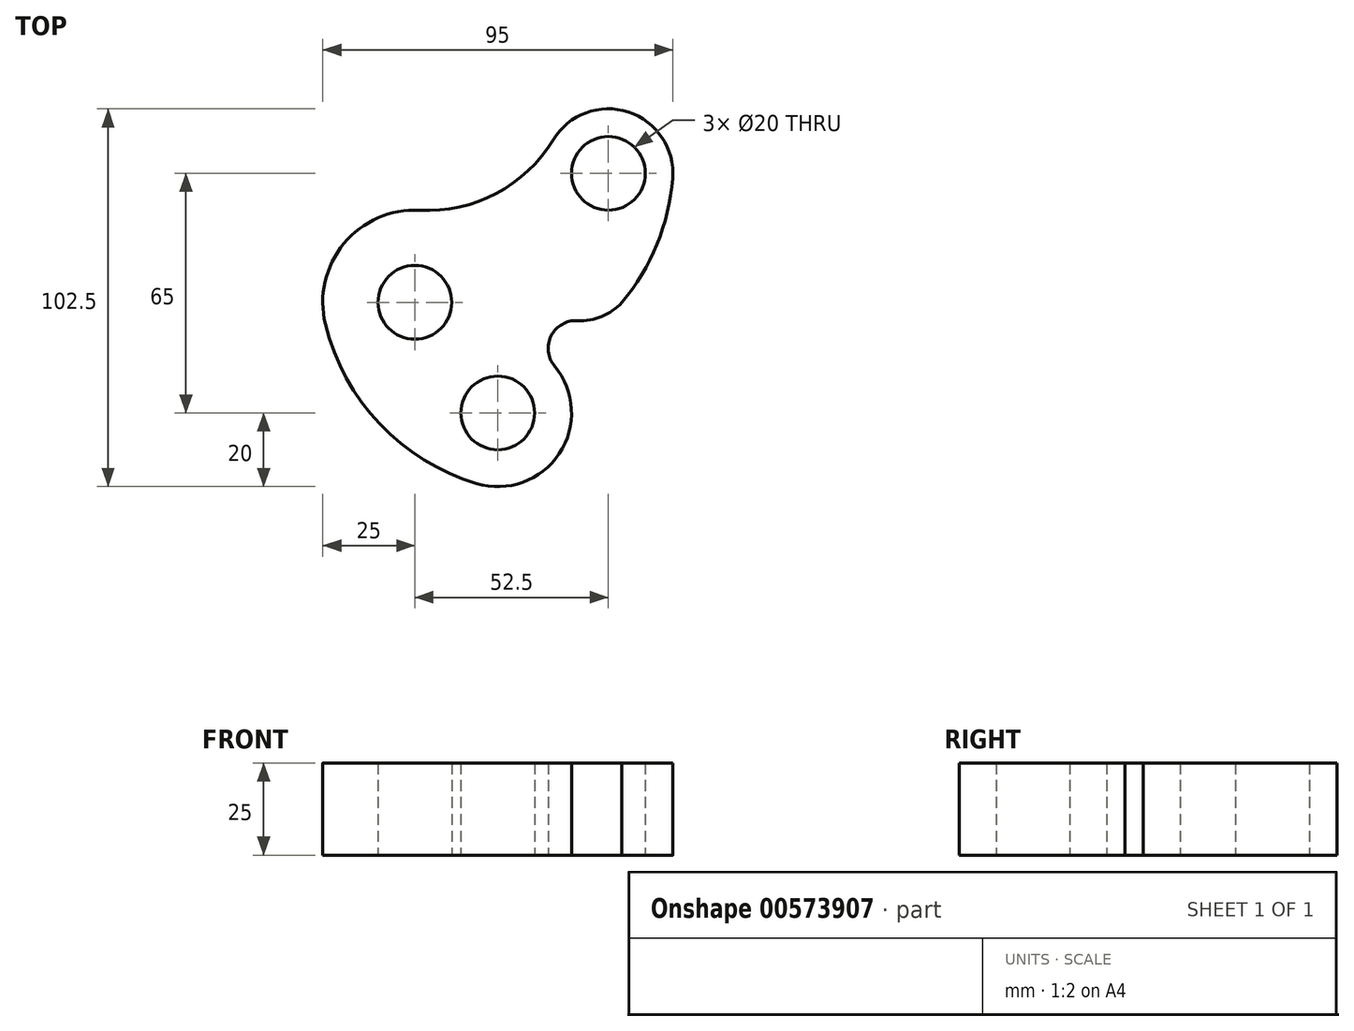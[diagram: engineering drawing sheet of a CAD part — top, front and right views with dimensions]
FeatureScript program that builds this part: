
annotation { "Feature Type Name" : "Feature", "Feature Type Description" : "" }
export const myFeature = defineFeature(function(context is Context, id is Id, definition is map)
    precondition{}
    {
        {
            var Q0;
            Q0=qCreatedBy(makeId("Top.planeOp"),FACE);
            var sketch = newSketch(context, id + "F0", { "sketchPlane" : qUnion([Q0])});
            skCircle(sketch, "E0", {"center": v(0, 0) * mm, "radius": 10 * mm});
            skArc(sketch, "E1", {"start": v(1.3, 24.97) * mm, "mid": v(-19.26, 15.94) * mm, "end": v(-24.28, -5.94) * mm});
            skCircle(sketch, "E2", {"center": v(52.5, 35) * mm, "radius": 10 * mm});
            skArc(sketch, "E3", {"start": v(69.94, 33.57) * mm, "mid": v(57.91, 51.64) * mm, "end": v(37.55, 44.1) * mm});
            skCircle(sketch, "E4", {"center": v(22.5, -30) * mm, "radius": 10 * mm});
            skArc(sketch, "E5", {"start": v(16.75, -49.16) * mm, "mid": v(39.17, -41.05) * mm, "end": v(37.9, -17.24) * mm});
            skArc(sketch, "E6", {"start": v(-24.28, -5.94) * mm, "mid": v(-9.51, -33) * mm, "end": v(16.75, -49.16) * mm});
            skArc(sketch, "E7", {"start": v(1.3, 24.97) * mm, "mid": v(22.07, 29.54) * mm, "end": v(37.55, 44.1) * mm});
            skArc(sketch, "E8", {"start": v(44.12, -4.97) * mm, "mid": v(51.33, -3.6) * mm, "end": v(57.03, 1.04) * mm});
            skArc(sketch, "E9", {"start": v(56.18, 0) * mm, "mid": v(65.66, 15.72) * mm, "end": v(69.94, 33.57) * mm});
            skArc(sketch, "E10", {"start": v(44.12, -4.97) * mm, "mid": v(37, -9.07) * mm, "end": v(37.9, -17.24) * mm});
            skSolve(sketch);
        }
        {
            var Q0;
            Q0=makeQuery(id+"F0.imprint","IMPRINT",FACE,{"disambiguationData":[TD([[makeQuery(id+"F0.imprint","IMPRINT",EDGE,{"derivedFrom":sQuery(id+"F0.wireOp",EDGE,"E0")}),-1.0]])]});
            extrude(context, id + "F1", {"entities" : qUnion([Q0]), "depth" : 25 * mm, "offsetDistance" : 25 * mm});
        }
    });
